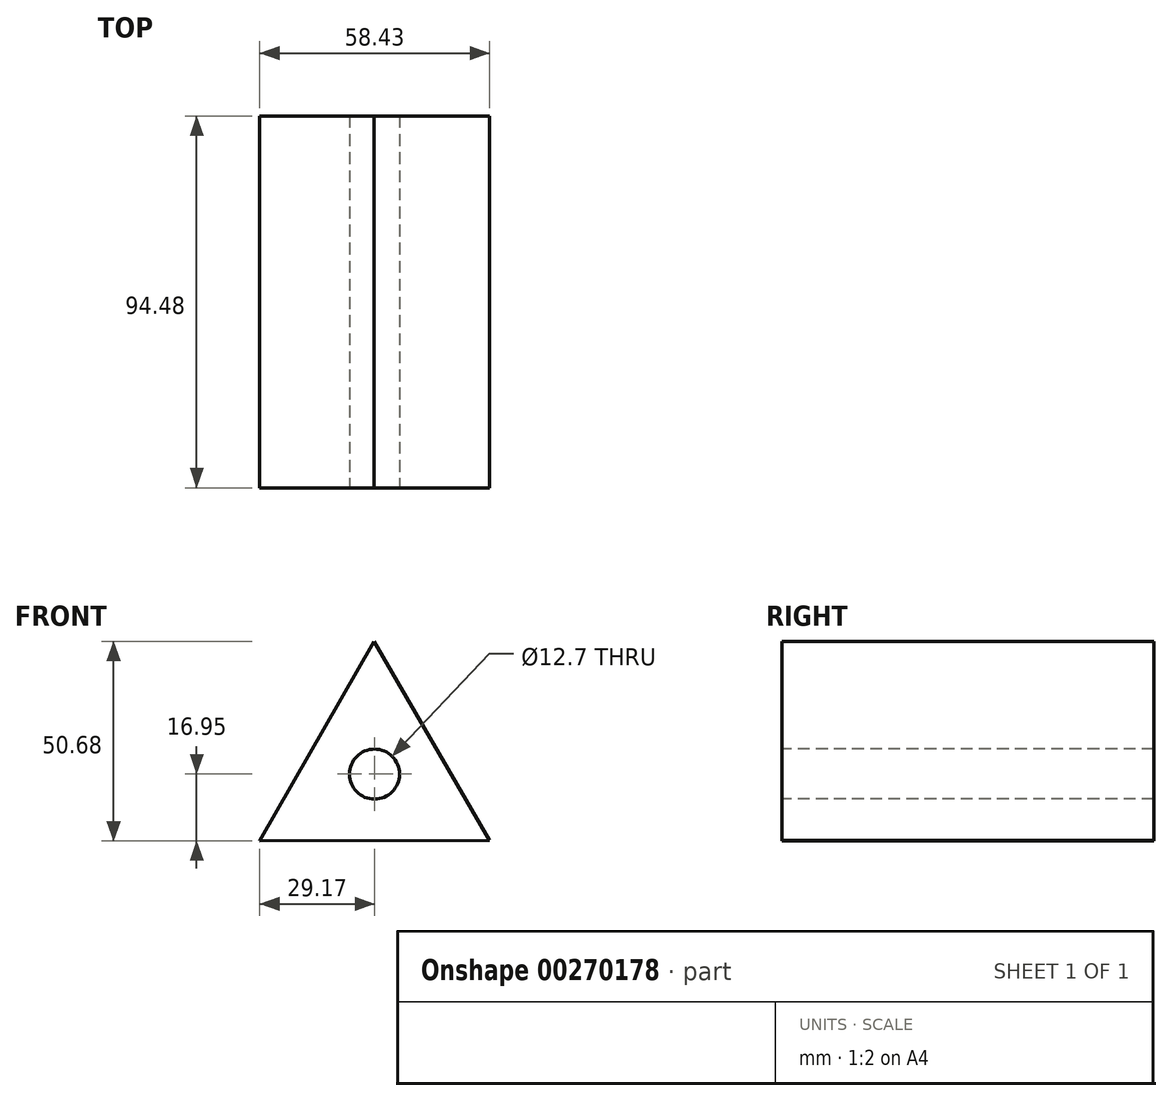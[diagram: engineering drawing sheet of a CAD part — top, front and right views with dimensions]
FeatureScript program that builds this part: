
annotation { "Feature Type Name" : "Feature", "Feature Type Description" : "" }
export const myFeature = defineFeature(function(context is Context, id is Id, definition is map)
    precondition{}
    {
        {
            var Q0;
            Q0=qCreatedBy(makeId("Front.planeOp"),FACE);
            var sketch = newSketch(context, id + "F0", { "sketchPlane" : qUnion([Q0])});
            skCircle(sketch, "E0.cCircle", {"center": v(0, 0) * mm, "radius": 16.87 * mm, "construction": true});
            skLineSegment(sketch, "E0.0", {"start": v(-0.1, 33.73) * mm, "end": v(29.26, -16.78) * mm});
            skLineSegment(sketch, "E0.1", {"start": v(29.26, -16.78) * mm, "end": v(-29.17, -16.95) * mm});
            skLineSegment(sketch, "E0.2", {"start": v(-29.17, -16.95) * mm, "end": v(-0.1, 33.73) * mm});
            skPoint(sketch, "E0.0.midPoint", {"position": v(14.58, 8.47) * mm});
            skSolve(sketch);
        }
        {
            var Q0;
            Q0 = qSketchRegion(id + "F0", true);
            extrude(context, id + "F1", {"entities" : qUnion([Q0]), "endBound" : BoundingType.SYMMETRIC, "oppositeDirection" : true, "depth" : 94.49 * mm});
        }
        {
            var Q0;
            Q0=makeQuery(id+"F1.opExtrude","CAP_FACE",FACE,{"disambiguationData":[OSD([sQuery(id+"F0.wireOp",EDGE,"E0.0"),sQuery(id+"F0.wireOp",EDGE,"E0.1"),sQuery(id+"F0.wireOp",EDGE,"E0.2")])],"isStart":true});
            var sketch = newSketch(context, id + "F2", { "sketchPlane" : qUnion([Q0])});
            skCircle(sketch, "E1", {"center": v(0, 0) * mm, "radius": 6.35 * mm});
            skSolve(sketch);
        }
        {
            var Q0;
            Q0=makeQuery(id+"F2.imprint","IMPRINT",FACE,{"disambiguationData":[TD([[makeQuery(id+"F2.imprint","IMPRINT",EDGE,{"derivedFrom":sQuery(id+"F2.wireOp",EDGE,"E1")}),1.0]])]});
            var Q1;
            Q1=sQuery(id+"F2.wireOp",EDGE,"E1");
            extrude(context, id + "F3", {"entities" : qUnion([Q0]), "operationType" : NewBodyOperationType.REMOVE, "surfaceEntities" : qUnion([Q1]), "endBound" : BoundingType.THROUGH_ALL, "oppositeDirection" : true, "depth" : 25.4 * mm});
        }
    });
